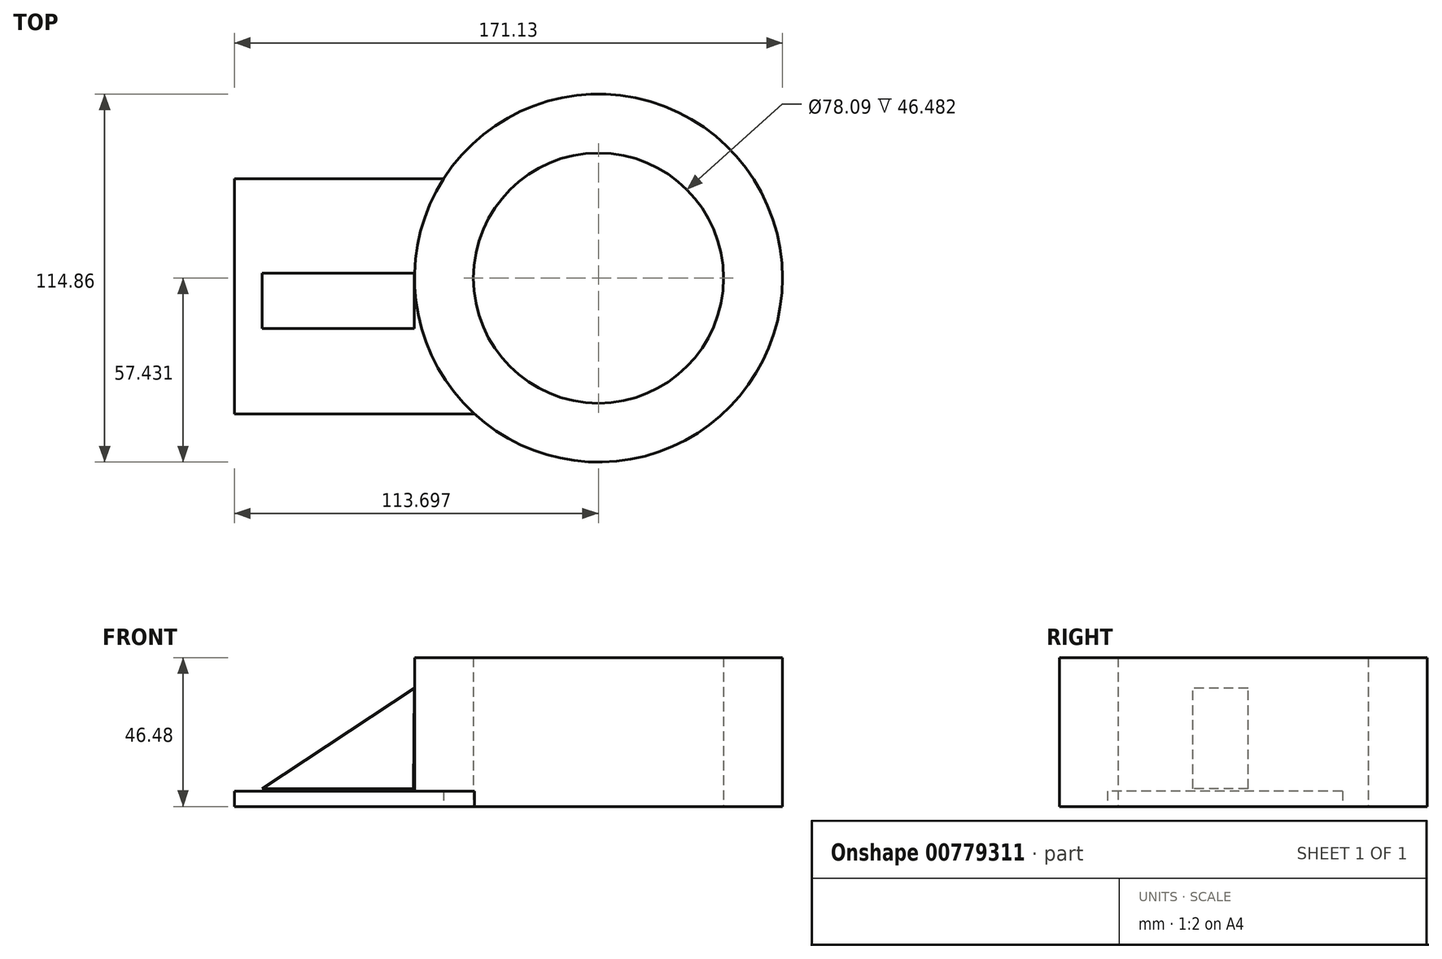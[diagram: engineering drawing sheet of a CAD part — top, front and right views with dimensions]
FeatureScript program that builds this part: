
annotation { "Feature Type Name" : "Feature", "Feature Type Description" : "" }
export const myFeature = defineFeature(function(context is Context, id is Id, definition is map)
    precondition{}
    {
        {
            var Q0;
            Q0=qCreatedBy(makeId("Top.planeOp"),FACE);
            var sketch = newSketch(context, id + "F0", { "sketchPlane" : qUnion([Q0])});
            skLineSegment(sketch, "E0.bottom", {"start": v(-76.55, 46.77) * mm, "end": v(-11.21, 46.77) * mm});
            skLineSegment(sketch, "E0.top", {"start": v(-76.55, -26.62) * mm, "end": v(-1.58, -26.62) * mm});
            skLineSegment(sketch, "E0.left", {"start": v(-76.55, 46.77) * mm, "end": v(-76.55, -26.62) * mm});
            skCircle(sketch, "E1", {"center": v(37.15, 15.8) * mm, "radius": 57.43 * mm});
            skCircle(sketch, "E2", {"center": v(37.15, 15.8) * mm, "radius": 39.04 * mm});
            skSolve(sketch);
        }
        {
            var Q0;
            Q0=makeQuery(id+"F0.imprint","IMPRINT",FACE,{"disambiguationData":[TD([[makeQuery(id+"F0.imprint","IMPRINT",EDGE,{"derivedFrom":sQuery(id+"F0.wireOp",EDGE,"E2")}),-1.0]])]});
            extrude(context, id + "F1", {"entities" : qUnion([Q0]), "depth" : 46.48 * mm, "offsetDistance" : 25.4 * mm});
        }
        {
            var Q0;
            {var subQ0=sQuery(id+"F0.wireOp",EDGE,"E0.bottom");Q0=makeQuery(id+"F0.imprint","IMPRINT",FACE,{"disambiguationData":[TD([[makeQuery(id+"F0.imprint","IMPRINT",EDGE,{"derivedFrom":subQ0}),-1.0]])]});}
            extrude(context, id + "F2", {"entities" : qUnion([Q0]), "operationType" : NewBodyOperationType.ADD, "depth" : 4.83 * mm, "offsetDistance" : 25.4 * mm});
        }
        {
            var Q0;
            Q0=qCreatedBy(makeId("Front.planeOp"),FACE);
            var sketch = newSketch(context, id + "F3", { "sketchPlane" : qUnion([Q0])});
            skLineSegment(sketch, "E3", {"start": v(-20.31, 36.85) * mm, "end": v(-67.84, 5.56) * mm});
            skLineSegment(sketch, "E4", {"start": v(-67.84, 5.56) * mm, "end": v(-20.61, 5.56) * mm});
            skLineSegment(sketch, "E5", {"start": v(-20.61, 5.56) * mm, "end": v(-20.31, 36.85) * mm});
            skSolve(sketch);
        }
        {
            var Q0;
            Q0=makeQuery(id+"F3.imprint","IMPRINT",FACE,{"disambiguationData":[TD([[makeQuery(id+"F3.imprint","IMPRINT",EDGE,{"derivedFrom":sQuery(id+"F3.wireOp",EDGE,"E3")}),1.0]])]});
            extrude(context, id + "F4", {"entities" : qUnion([Q0]), "oppositeDirection" : true, "depth" : 17.27 * mm, "offsetDistance" : 25.4 * mm});
        }
    });
